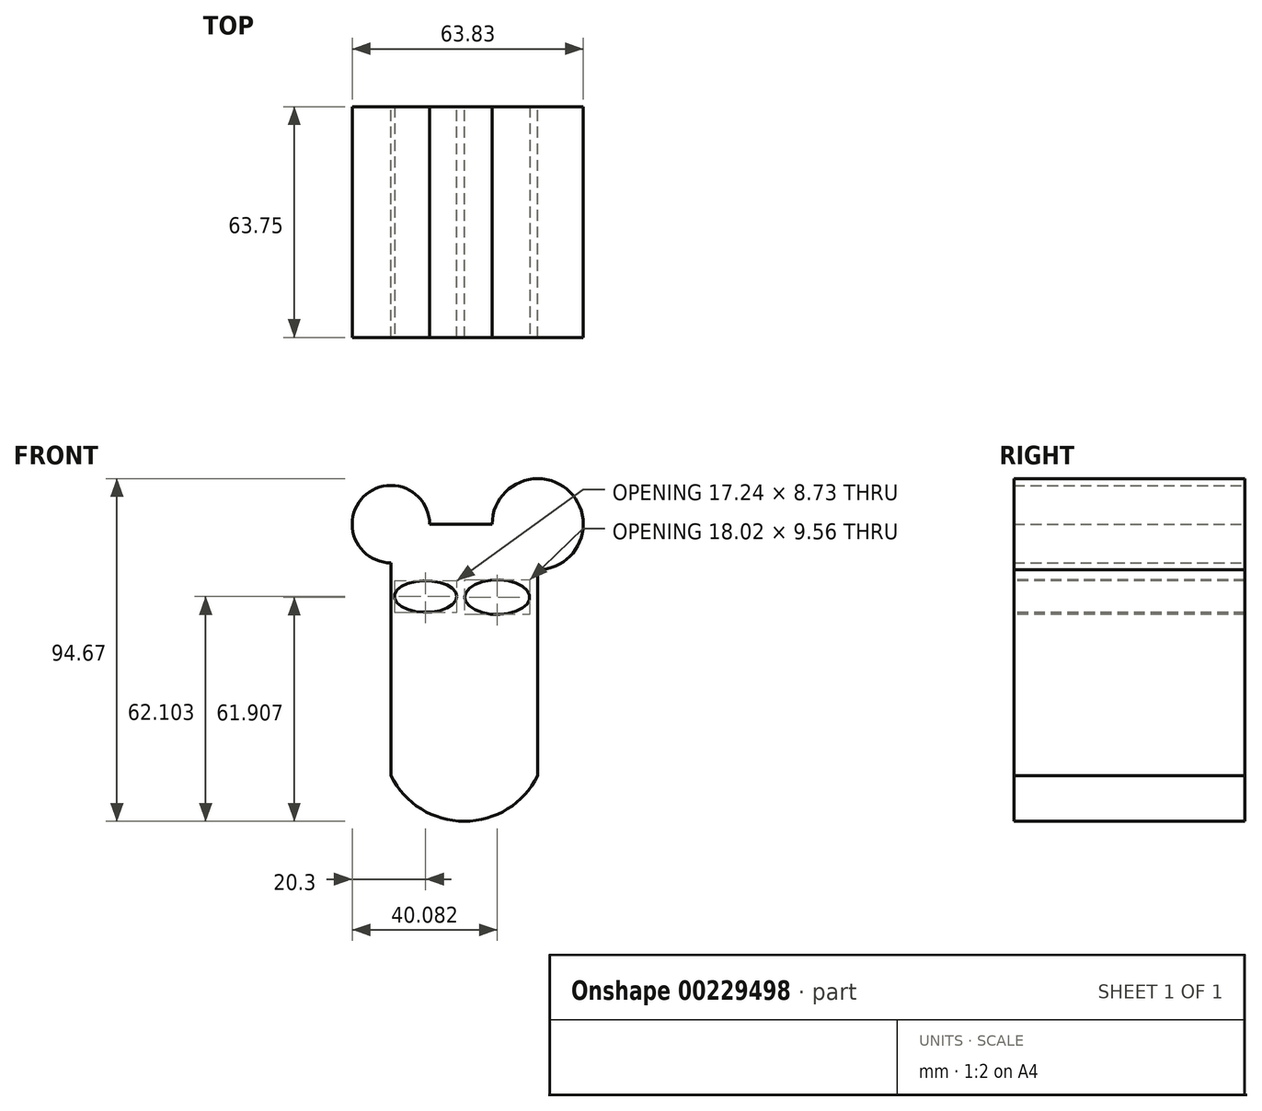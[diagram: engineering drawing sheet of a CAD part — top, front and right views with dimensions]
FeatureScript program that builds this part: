
annotation { "Feature Type Name" : "Feature", "Feature Type Description" : "" }
export const myFeature = defineFeature(function(context is Context, id is Id, definition is map)
    precondition{}
    {
        {
            var Q0;
            Q0=qCreatedBy(makeId("Front.planeOp"),FACE);
            var sketch = newSketch(context, id + "F0", { "sketchPlane" : qUnion([Q0])});
            skLineSegment(sketch, "E0.bottom", {"start": v(-18.6, 35.94) * mm, "end": v(21.94, 35.94) * mm});
            skLineSegment(sketch, "E0.top", {"start": v(-18.6, -33.6) * mm, "end": v(21.94, -33.6) * mm});
            skLineSegment(sketch, "E0.left", {"start": v(-18.6, 35.94) * mm, "end": v(-18.6, -33.6) * mm});
            skLineSegment(sketch, "E0.right", {"start": v(21.94, 35.94) * mm, "end": v(21.94, -33.6) * mm});
            skCircle(sketch, "E1", {"center": v(-18.6, 35.94) * mm, "radius": 10.7 * mm});
            skCircle(sketch, "E2", {"center": v(21.94, 35.94) * mm, "radius": 12.59 * mm});
            skEllipse(sketch, "E3", {"center": v(-9, 15.96) * mm, "majorRadius": 8.62 * mm, "minorRadius": 4.36 * mm, "majorAxis": v(1, 0)});
            skEllipse(sketch, "E4", {"center": v(10.77, 15.77) * mm, "majorRadius": 9 * mm, "minorRadius": 4.78 * mm, "majorAxis": v(-1, 0)});
            skArc(sketch, "E5", {"start": v(-18.6, -33.6) * mm, "mid": v(1.66, -46.14) * mm, "end": v(21.94, -33.6) * mm});
            skArc(sketch, "E6", {"start": v(-18.6, -33.6) * mm, "mid": v(1.66, -37.95) * mm, "end": v(21.94, -33.6) * mm});
            skSolve(sketch);
        }
        {
            var Q0;
            Q0 = qSketchRegion(id + "F0", true);
            extrude(context, id + "F1", {"entities" : qUnion([Q0]), "depth" : 38.35 * mm});
        }
        {
            var Q0;
            Q0=makeQuery(id+"F1.opExtrude","CAP_FACE",FACE,{"disambiguationData":[OSD([sQuery(id+"F0.wireOp",EDGE,"E0.bottom"),sQuery(id+"F0.wireOp",EDGE,"E0.left"),sQuery(id+"F0.wireOp",EDGE,"E0.right"),sQuery(id+"F0.wireOp",EDGE,"E1"),sQuery(id+"F0.wireOp",EDGE,"E2"),sQuery(id+"F0.wireOp",EDGE,"E3"),sQuery(id+"F0.wireOp",EDGE,"E4"),sQuery(id+"F0.wireOp",EDGE,"E5")])],"isStart":false});
            var sketch = newSketch(context, id + "F2", { "sketchPlane" : qUnion([Q0])});
            skSolve(sketch);
        }
        {
            var Q0;
            Q0=makeQuery(id+"F2.imprint","IMPRINT",FACE,{"disambiguationData":[TD([[makeQuery(id+"F2.imprint","IMPRINT",EDGE,{"derivedFrom":makeQuery(id+"F1.opExtrude","CAP_EDGE",EDGE,{"disambiguationData":[OSD([sQuery(id+"F0.wireOp",EDGE,"E0.bottom")])],"isStart":false})}),-1.0]])]});
            extrude(context, id + "F3", {"entities" : qUnion([Q0]), "operationType" : NewBodyOperationType.ADD, "depth" : 25.4 * mm});
        }
    });
